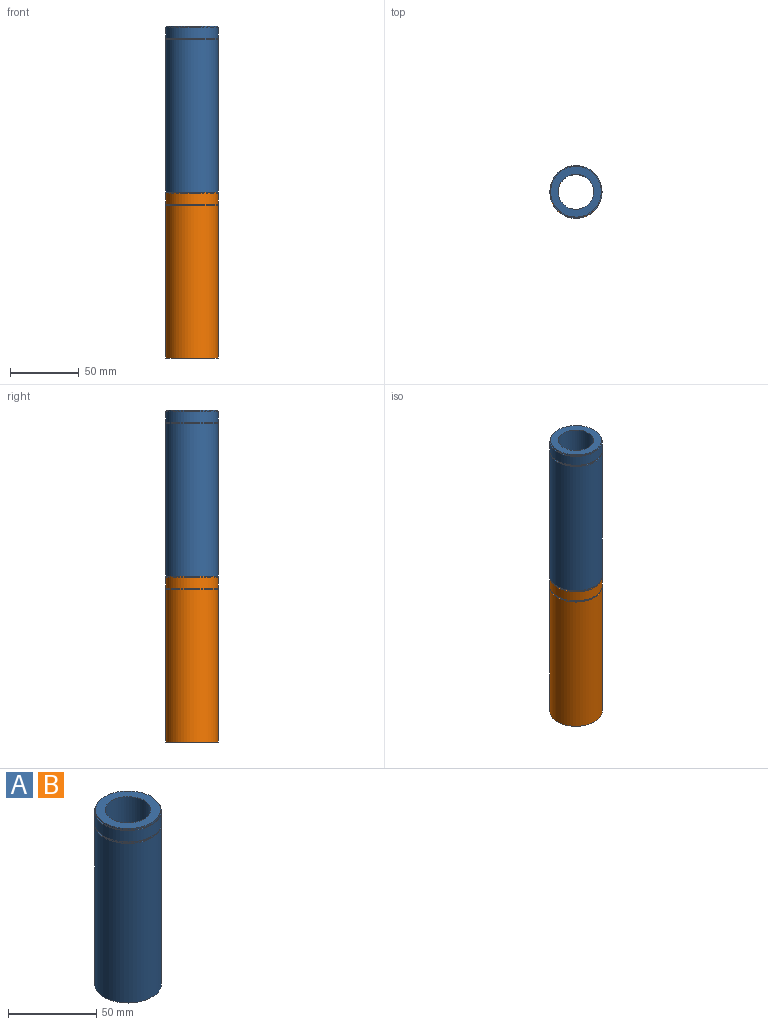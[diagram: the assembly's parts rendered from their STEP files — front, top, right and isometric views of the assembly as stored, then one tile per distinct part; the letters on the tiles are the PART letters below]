
ASSEMBLY  parts=2 mates=1
PART A: 10 faces, bbox 38x38x121 mm
  f0: cylinder r=19mm len=111mm, axis (0,0,-1), area 13251.2mm2, adj f1,f2
  f1: plane 38x38mm, normal (0,0,1), area 58.9mm2, adj f0,f3
  f2: plane 38x38mm, normal (0,0,-1), area 611.3mm2, adj f0,f4
  f3: cylinder r=18.5mm len=37mm, axis (0,0,-1), area 116.2mm2, adj f1,f7
  f4: cylinder r=12.9mm len=121mm, axis (0,0,1), area 9807.4mm2, adj f2,f9
  f5: cylinder r=19mm len=38mm, axis (0,0,-1), area 955mm2, adj f6,f7
  f6: plane 38x38mm, normal (0,0,1), area 58.9mm2, adj f5,f8
  f7: plane 38x38mm, normal (0,0,-1), area 58.9mm2, adj f3,f5
  f8: cylinder r=18.5mm len=37mm, axis (0,0,-1), area 116.2mm2, adj f6,f9
  f9: plane 37x37mm, normal (0,0,1), area 552.4mm2, adj f4,f8
PART B: same geometry as A
PLACE A t=(76.3,0,-120)mm
PLACE B t=(76.3,0,-241)mm
MATE fastened B.f4 <-> A.f4  axis (0,0,1) through (76.3,0,-120)mm
